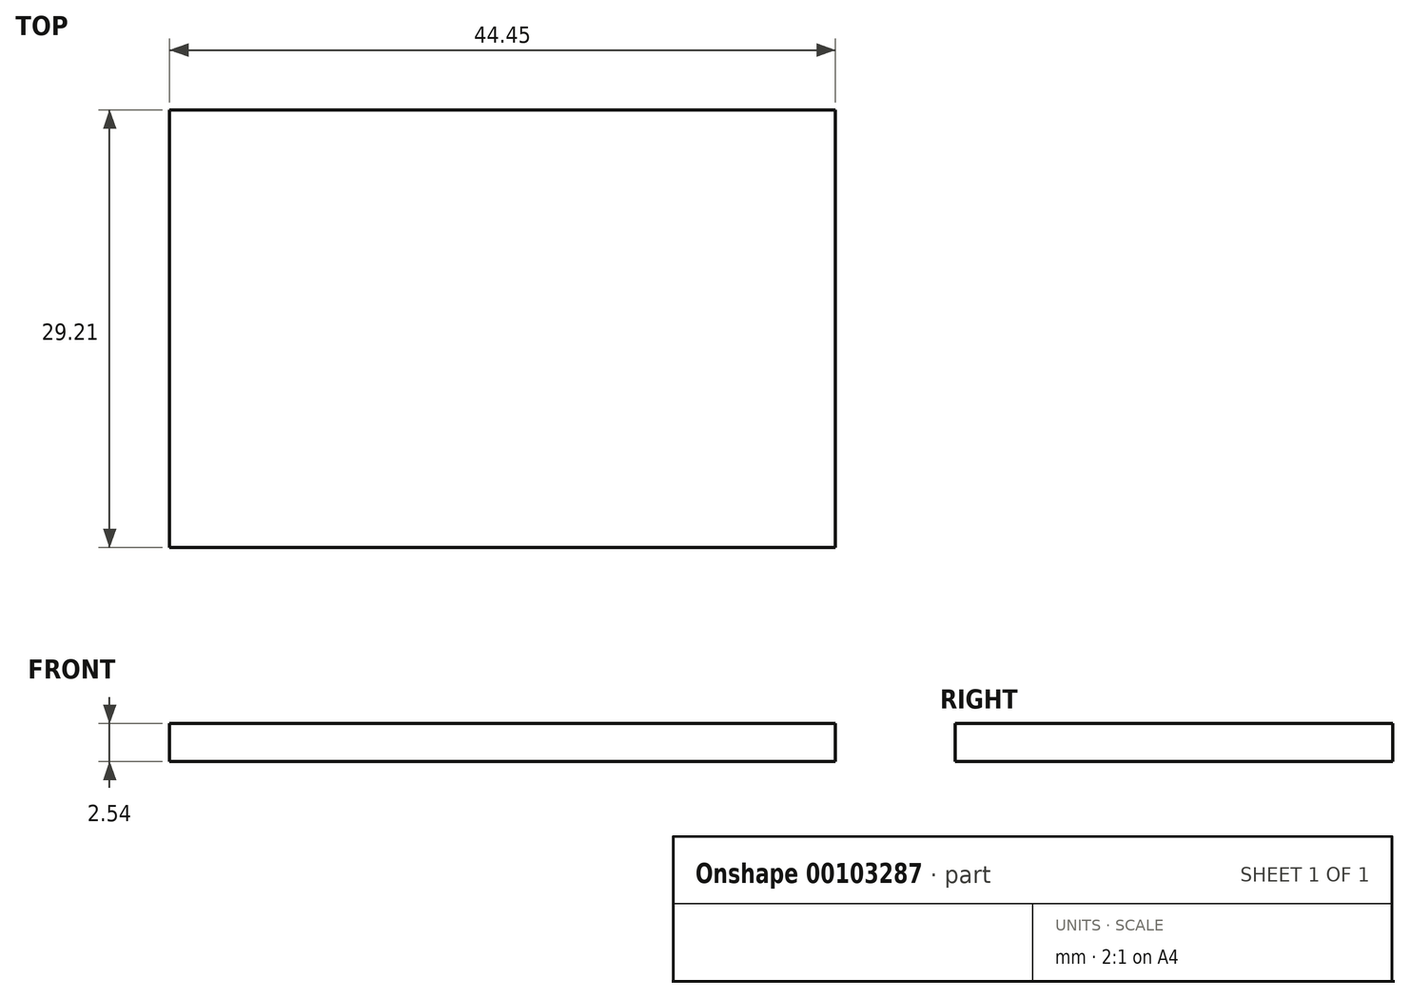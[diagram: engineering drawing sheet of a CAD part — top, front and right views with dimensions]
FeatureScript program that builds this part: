
annotation { "Feature Type Name" : "Feature", "Feature Type Description" : "" }
export const myFeature = defineFeature(function(context is Context, id is Id, definition is map)
    precondition{}
    {
        {
            var Q0;
            Q0=qCreatedBy(makeId("Top.planeOp"),FACE);
            var sketch = newSketch(context, id + "F0", { "sketchPlane" : qUnion([Q0])});
            skLineSegment(sketch, "E0.bottom", {"start": v(0, 0) * mm, "end": v(44.45, 0) * mm});
            skLineSegment(sketch, "E0.top", {"start": v(0, 29.21) * mm, "end": v(44.45, 29.21) * mm});
            skLineSegment(sketch, "E0.left", {"start": v(0, 0) * mm, "end": v(0, 29.21) * mm});
            skLineSegment(sketch, "E0.right", {"start": v(44.45, 0) * mm, "end": v(44.45, 29.21) * mm});
            skSolve(sketch);
        }
        {
            var Q0;
            Q0=makeQuery(id+"F0.imprint","IMPRINT",FACE,{"disambiguationData":[TD([[makeQuery(id+"F0.imprint","IMPRINT",EDGE,{"derivedFrom":sQuery(id+"F0.wireOp",EDGE,"E0.bottom")}),1.0]])]});
            extrude(context, id + "F1", {"entities" : qUnion([Q0]), "depth" : 2.54 * mm});
        }
    });
